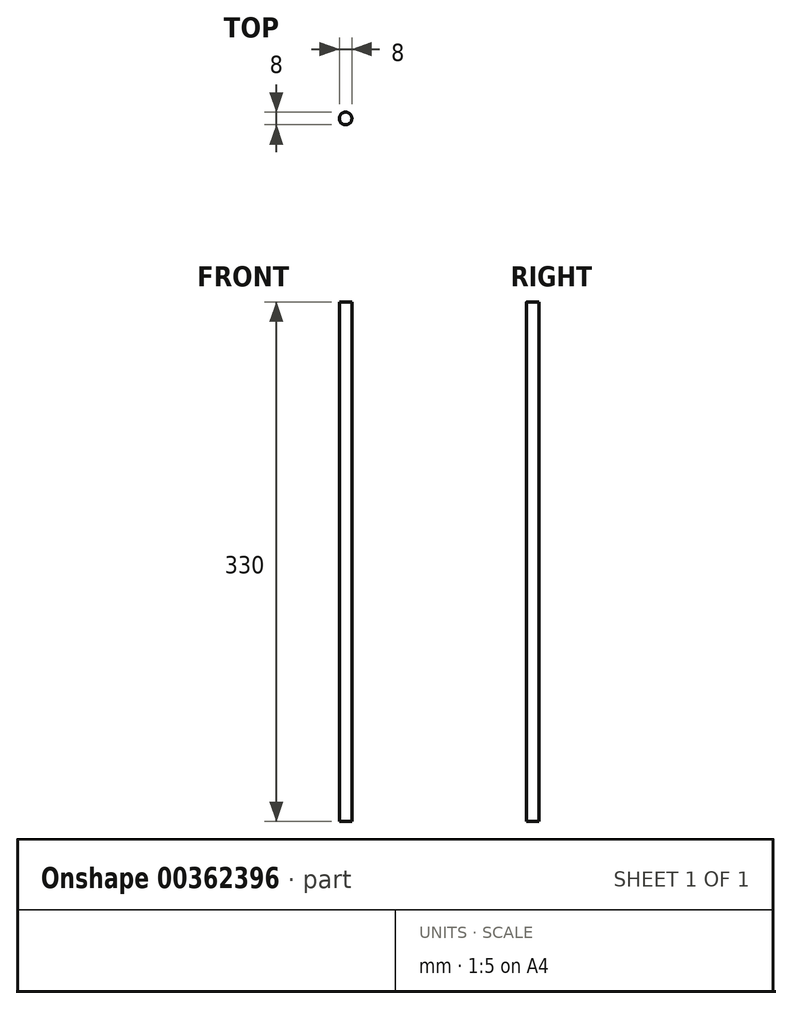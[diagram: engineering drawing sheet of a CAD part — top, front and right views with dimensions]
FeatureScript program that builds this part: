
annotation { "Feature Type Name" : "Feature", "Feature Type Description" : "" }
export const myFeature = defineFeature(function(context is Context, id is Id, definition is map)
    precondition{}
    {
        {
            var Q0;
            Q0=qCreatedBy(makeId("Top.planeOp"),FACE);
            var sketch = newSketch(context, id + "F0", { "sketchPlane" : qUnion([Q0])});
            skCircle(sketch, "E0", {"center": v(0, 0.15) * mm, "radius": 4 * mm});
            skSolve(sketch);
        }
        {
            var Q0;
            Q0=qSketchRegion(id+"F0",true);
            extrude(context, id + "F1", {"entities" : qUnion([Q0]), "depth" : 330 * mm});
        }
    });
